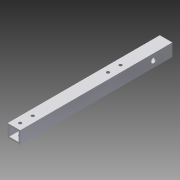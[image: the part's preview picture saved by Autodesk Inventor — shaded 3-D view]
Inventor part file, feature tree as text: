
AUTODESK INVENTOR PART (.ipt)
format: ipt  version: 2015 SP1 (Build 190203100, 203)  size: 132,608 bytes
history: native  units: in
note: dims shown in document units (in); Inventor stores cm internally (conversion verified against a paired STEP export)
features: sketch x4, extrude x2, hole x2
ambient origin geometry x8: Origin, YZ Plane, XZ Plane, XY Plane, X Axis, Y Axis, Z Axis, Center Point
bodies: Solid1 (feature_tree)
feature tree (8):
  extrude  "Extrusion1"  Depth=1.0in
  hole  "Hole1"  [1 undecoded]
  hole  "Hole2"  [1 undecoded]
  extrude  "Extrusion2"  Depth=1.0in
  sketch  "Sketch1"  dims[d0=1.0in d1=1.0in]
  sketch  "Sketch2"  dims[d2=0.75in d3=0.75in]
  sketch  "Sketch3"  dims[d4=0.125in d5=0.125in]
  sketch  "Sketch4"  dims[d6=12.125in d7=0.0in d8=0.5in d9=0.5in d11=0.5in d16=0.5in d17=0.5in d18=0.25in d19=0.75in d20=0.375in d21=0.25in d22=0.5635in d23=1.0in d24=0.8108in d25=1.5in d26=0.5in d27=0.375in d28=0.75in d29=0.375in d30=0.25in d31=0.5635in d32=1.0in d33=0.8108in d34=6.0in d35=1.0in d36=1.0in d37=0.5in d38=0.5in d39=0.0in]
note: 2 required parameter values undecoded (feature->parameter linkage not recoverable at this tier; creation-order binding heuristic only, values carry confidence <= 0.55)
